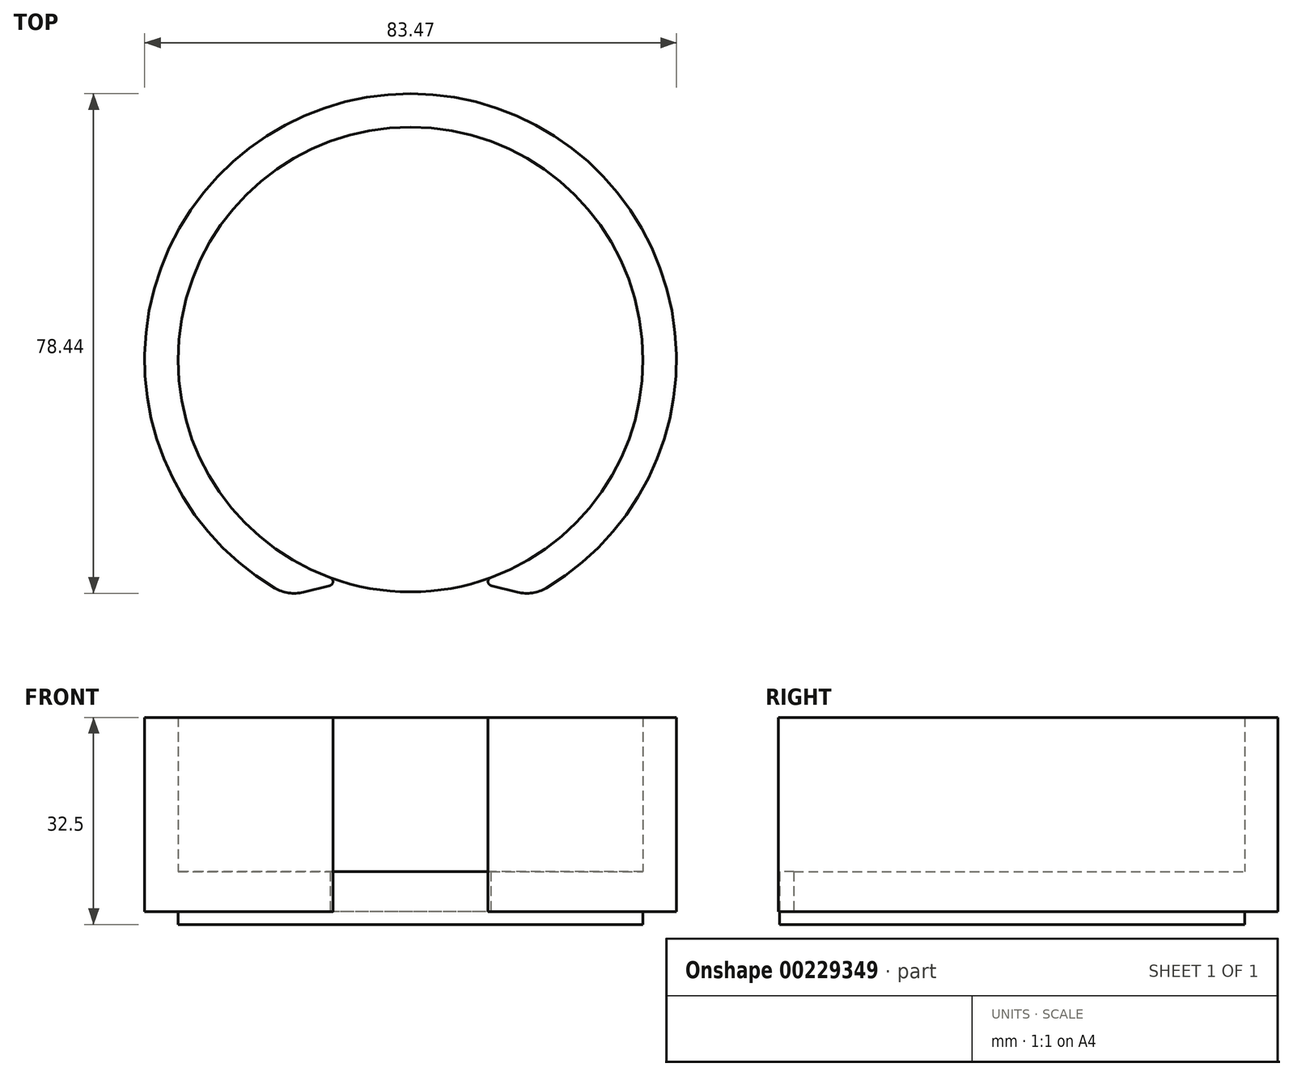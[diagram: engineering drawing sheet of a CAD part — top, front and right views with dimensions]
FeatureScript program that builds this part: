
annotation { "Feature Type Name" : "Feature", "Feature Type Description" : "" }
export const myFeature = defineFeature(function(context is Context, id is Id, definition is map)
    precondition{}
    {
        {
            var Q0;
            Q0=qCreatedBy(makeId("Top.planeOp"),FACE);
            var sketch = newSketch(context, id + "F0", { "sketchPlane" : qUnion([Q0])});
            skCircle(sketch, "E0", {"center": v(0, 0) * mm, "radius": 41.73 * mm});
            skCircle(sketch, "E1", {"center": v(0, 0) * mm, "radius": 36.5 * mm});
            skLineSegment(sketch, "E2", {"start": v(0, 41.73) * mm, "end": v(0, -52.56) * mm, "construction": true});
            skLineSegment(sketch, "E3", {"start": v(0, 0) * mm, "end": v(-10.5, -34.96) * mm});
            skLineSegment(sketch, "E4.MirrorCS", {"start": v(0, 0) * mm, "end": v(10.5, -34.96) * mm});
            skLineSegment(sketch, "E5", {"start": v(-10.5, -34.96) * mm, "end": v(-19.1, -37.1) * mm});
            skLineSegment(sketch, "E6.MirrorCS", {"start": v(10.5, -34.96) * mm, "end": v(19.1, -37.1) * mm});
            skSolve(sketch);
        }
        {
            var Q0;
            {var subQ0=sQuery(id+"F0.wireOp",EDGE,"E5");Q0=makeQuery(id+"F0.imprint","IMPRINT",FACE,{"disambiguationData":[TD([[makeQuery(id+"F0.imprint","IMPRINT",EDGE,{"derivedFrom":subQ0}),-1.0]])]});}
            extrude(context, id + "F1", {"entities" : qUnion([Q0]), "depth" : 30.5 * mm});
        }
        {
            var Q0;
            Q0=makeQuery(id+"F1.opExtrude","SWEPT_EDGE",EDGE,{"disambiguationData":[OSD([sQuery(id+"F0.wireOp",EDGE,"E1"),sQuery(id+"F0.wireOp",EDGE,"E3"),sQuery(id+"F0.wireOp",EDGE,"E5")])]});
            var Q1;
            Q1=makeQuery(id+"F1.opExtrude","SWEPT_EDGE",EDGE,{"disambiguationData":[OSD([sQuery(id+"F0.wireOp",EDGE,"E1"),sQuery(id+"F0.wireOp",EDGE,"E4.MirrorCS"),sQuery(id+"F0.wireOp",EDGE,"E6.MirrorCS")])]});
            fillet(context, id + "F2", {"entities" : qUnion([Q0, Q1]), "radius" : 0.65 * mm, "tangentPropagation" : true, "allowEdgeOverflow" : false});
        }
        {
            var Q0;
            Q0=makeQuery(id+"F1.opExtrude","SWEPT_EDGE",EDGE,{"disambiguationData":[OSD([sQuery(id+"F0.wireOp",EDGE,"E0"),sQuery(id+"F0.wireOp",EDGE,"E5")])]});
            var Q1;
            Q1=makeQuery(id+"F1.opExtrude","SWEPT_EDGE",EDGE,{"disambiguationData":[OSD([sQuery(id+"F0.wireOp",EDGE,"E0"),sQuery(id+"F0.wireOp",EDGE,"E6.MirrorCS")])]});
            fillet(context, id + "F3", {"entities" : qUnion([Q0, Q1]), "radius" : 6 * mm, "tangentPropagation" : true, "allowEdgeOverflow" : false});
        }
        {
            var Q0;
            {var subQ0=sQuery(id+"F0.wireOp",EDGE,"E3");Q0=makeQuery(id+"F0.imprint","IMPRINT",FACE,{"disambiguationData":[TD([[makeQuery(id+"F0.imprint","IMPRINT",EDGE,{"derivedFrom":subQ0}),-1.0]])]});}
            var Q1;
            {var subQ0=sQuery(id+"F0.wireOp",EDGE,"E3");Q1=makeQuery(id+"F0.imprint","IMPRINT",FACE,{"disambiguationData":[TD([[makeQuery(id+"F0.imprint","IMPRINT",EDGE,{"derivedFrom":subQ0}),1.0]])]});}
            extrude(context, id + "F4", {"entities" : qUnion([Q0, Q1]), "depth" : 6.28 * mm});
        }
        {
            var Q0;
            Q0=makeQuery(id+"F4.opExtrude","CAP_FACE",FACE,{"disambiguationData":[OSD([sQuery(id+"F0.wireOp",EDGE,"E1")])],"isStart":true});
            extrude(context, id + "F5", {"entities" : qUnion([Q0]), "operationType" : NewBodyOperationType.ADD, "depth" : 2 * mm});
        }
    });
